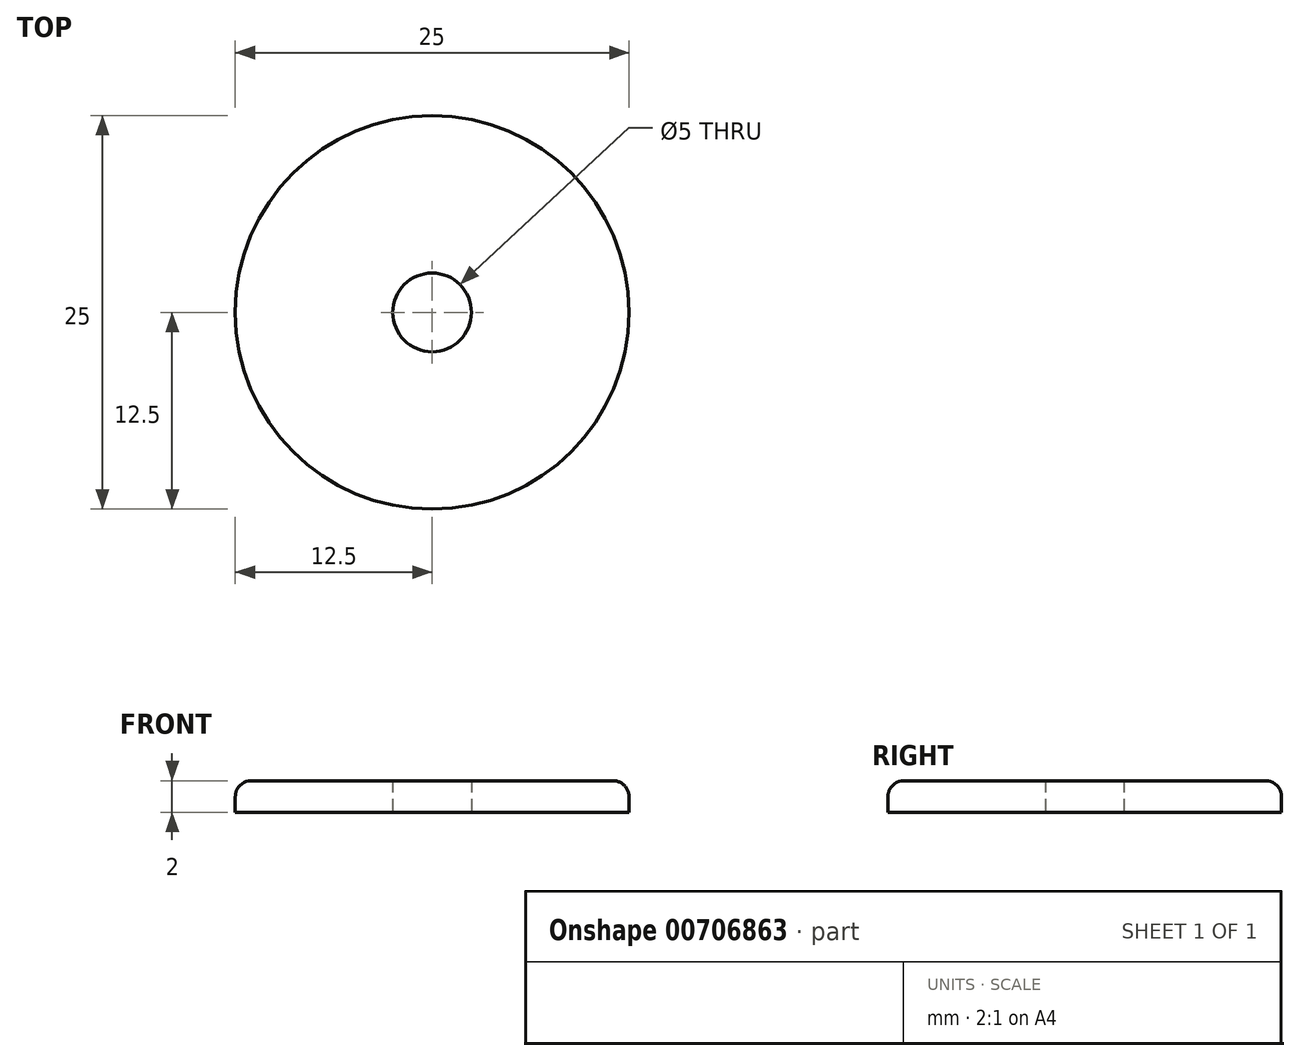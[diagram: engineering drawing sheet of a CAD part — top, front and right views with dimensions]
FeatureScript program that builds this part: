
annotation { "Feature Type Name" : "Feature", "Feature Type Description" : "" }
export const myFeature = defineFeature(function(context is Context, id is Id, definition is map)
    precondition{}
    {
        {
            var Q0;
            Q0=qCreatedBy(makeId("Top.planeOp"),FACE);
            var sketch = newSketch(context, id + "F0", { "sketchPlane" : qUnion([Q0])});
            skCircle(sketch, "E0", {"center": v(0, 0) * mm, "radius": 12.5 * mm});
            skSolve(sketch);
        }
        {
            var Q0;
            Q0 = qSketchRegion(id + "F0", true);
            extrude(context, id + "F1", {"entities" : qUnion([Q0]), "depth" : 2 * mm, "offsetDistance" : 25.4 * mm});
        }
        {
            var Q0;
            Q0=makeQuery(id+"F1.opExtrude","CAP_EDGE",EDGE,{"disambiguationData":[OSD([sQuery(id+"F0.wireOp",EDGE,"E0")])],"isStart":false});
            fillet(context, id + "F2", {"entities" : qUnion([Q0]), "radius" : 1 * mm, "tangentPropagation" : true, "allowEdgeOverflow" : false});
        }
        {
            var Q0;
            Q0=makeQuery(id+"F1.opExtrude","CAP_FACE",FACE,{"disambiguationData":[OSD([sQuery(id+"F0.wireOp",EDGE,"E0")])],"isStart":true});
            var sketch = newSketch(context, id + "F3", { "sketchPlane" : qUnion([Q0])});
            skCircle(sketch, "E1", {"center": v(0, 0) * mm, "radius": 2.5 * mm});
            skSolve(sketch);
        }
        {
            var Q0;
            Q0 = qSketchRegion(id + "F3", true);
            extrude(context, id + "F4", {"entities" : qUnion([Q0]), "operationType" : NewBodyOperationType.REMOVE, "oppositeDirection" : true, "depth" : 25.4 * mm, "offsetDistance" : 25.4 * mm});
        }
    });
